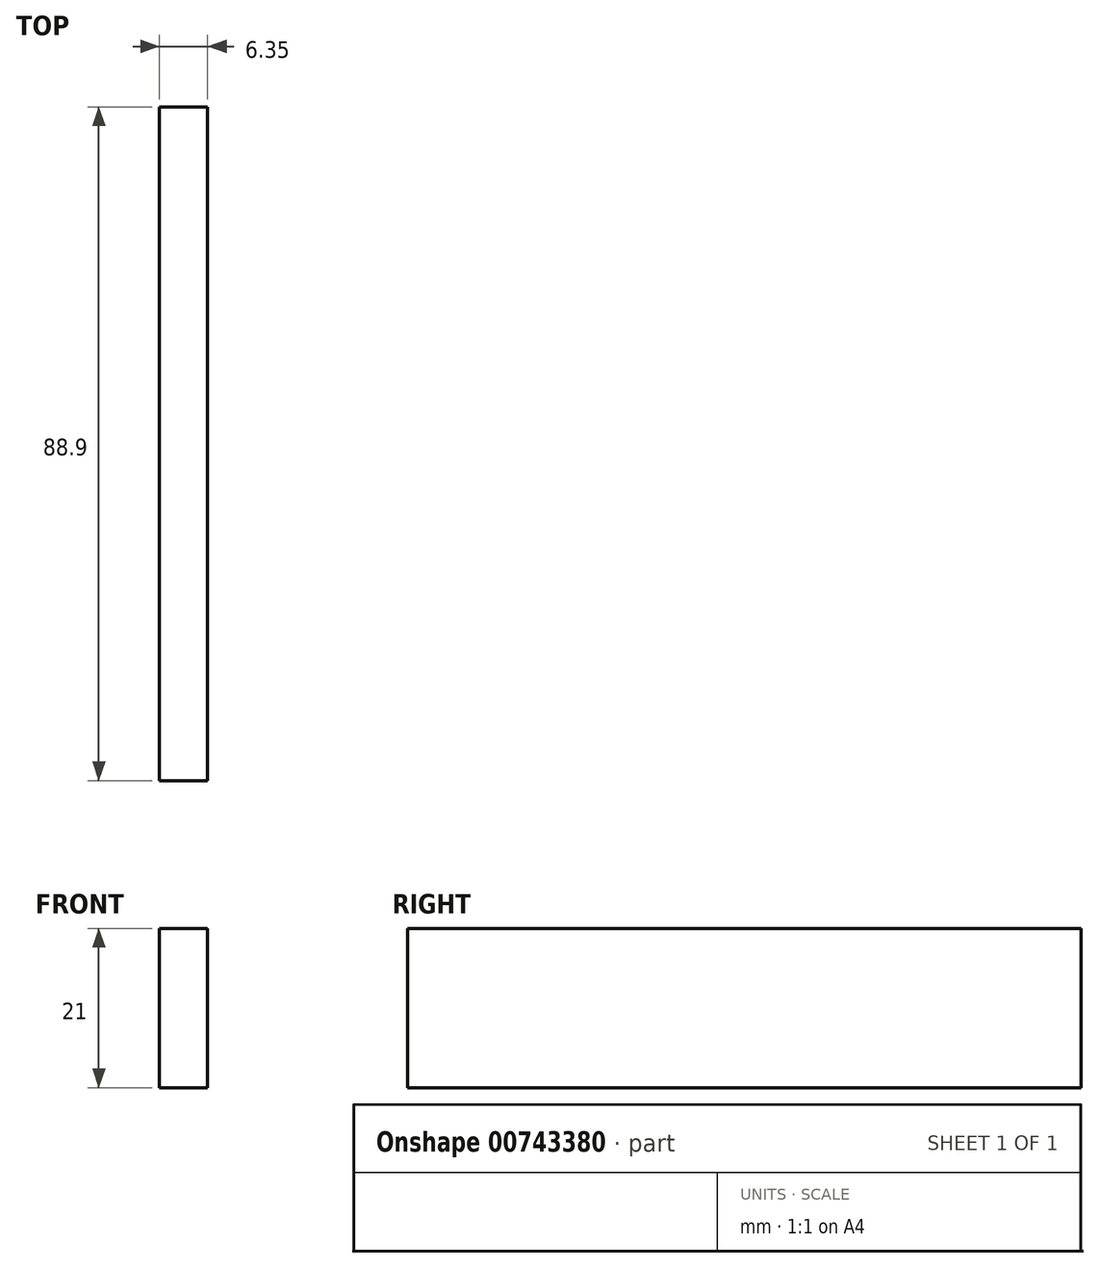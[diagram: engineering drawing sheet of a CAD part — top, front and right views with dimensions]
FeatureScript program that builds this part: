
annotation { "Feature Type Name" : "Feature", "Feature Type Description" : "" }
export const myFeature = defineFeature(function(context is Context, id is Id, definition is map)
    precondition{}
    {
        {
            var Q0;
            Q0=qCreatedBy(makeId("Top.planeOp"),FACE);
            var sketch = newSketch(context, id + "F0", { "sketchPlane" : qUnion([Q0])});
            skLineSegment(sketch, "E0.bottom", {"start": v(182.93, -44.45) * mm, "end": v(176.58, -44.45) * mm});
            skLineSegment(sketch, "E0.top", {"start": v(182.93, 44.45) * mm, "end": v(176.58, 44.45) * mm});
            skLineSegment(sketch, "E0.left", {"start": v(182.93, -44.45) * mm, "end": v(182.93, 44.45) * mm});
            skLineSegment(sketch, "E0.right", {"start": v(176.58, -44.45) * mm, "end": v(176.58, 44.45) * mm});
            skPoint(sketch, "E0.middle", {"position": v(179.75, 0) * mm});
            skSolve(sketch);
        }
        {
            var Q0;
            Q0 = qSketchRegion(id + "F0", true);
            extrude(context, id + "F1", {"entities" : qUnion([Q0]), "oppositeDirection" : true, "depth" : 21 * mm, "offsetDistance" : 25.4 * mm});
        }
    });
